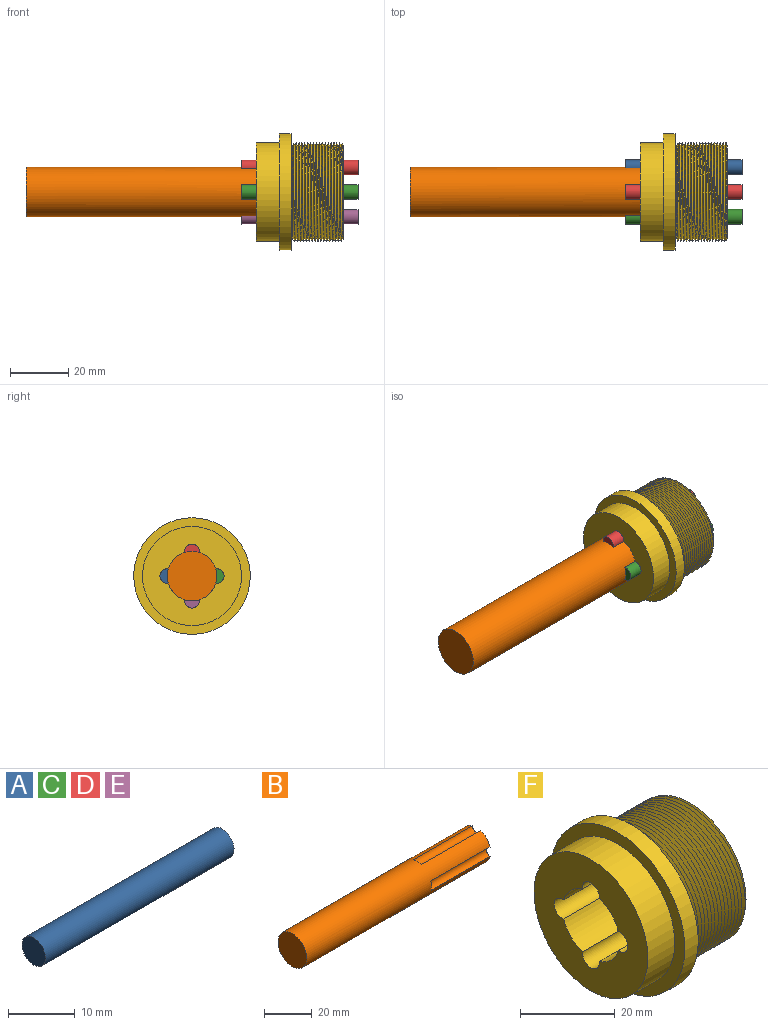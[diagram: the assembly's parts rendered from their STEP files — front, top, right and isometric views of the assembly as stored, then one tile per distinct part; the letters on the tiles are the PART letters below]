
ASSEMBLY  parts=6 mates=1
PART A: 3 faces, bbox 40x5x5 mm
  f0: cylinder r=2.5mm len=40mm, axis (-1,0,0), area 628.3mm2, adj f1,f2
  f1: plane 5x5mm, normal (1,0,0), area 19.6mm2, adj f0
  f2: plane 5x5mm, normal (-1,0,0), area 19.6mm2, adj f0
PART B: 11 faces, bbox 109x17x17 mm
  f0: plane 16.26x16.26mm, normal (1,0,0), area 190.2mm2, adj f1,f3,f5,f7,f9
  f1: cylinder r=8.5mm len=109mm, axis (-1,0,0), area 5118.8mm2, adj f0,f2,f3,f4,f5,f6,f7,f8
  f2: plane 17x17mm, normal (-1,0,0), area 227mm2, adj f1
  f3: cylinder r=2.5mm len=35mm, axis (1,0,0), area 249.1mm2, adj f0,f1,f4
  f4: plane 4.95x2.5mm, normal (1,0,0), area 9.2mm2, adj f1,f3
  f5: cylinder r=2.5mm len=35mm, axis (1,0,0), area 249.1mm2, adj f0,f1,f6
  f6: plane 4.95x2.5mm, normal (1,0,0), area 9.2mm2, adj f1,f5
  f7: cylinder r=2.5mm len=35mm, axis (1,0,0), area 249.1mm2, adj f0,f1,f8
  f8: plane 4.95x2.5mm, normal (1,0,0), area 9.2mm2, adj f1,f7
  f9: cylinder r=2.5mm len=35mm, axis (1,0,0), area 249.1mm2, adj f0,f1,f10
  f10: plane 4.95x2.5mm, normal (1,0,0), area 9.2mm2, adj f1,f9
PART C: same geometry as A
PART D: same geometry as A
PART E: same geometry as A
PART F: 19 faces, bbox 30.7x40x40 mm
  f0: plane 32x32mm, normal (1,0,0), area 535.5mm2, adj f3,f4,f5,f11,f12,f13,f14,f15
  f1: bspline ~39.26x34mm, area 1956.4mm2, adj f2,f16,f17
  f2: bspline ~39.26x34mm, area 1970.7mm2, adj f1,f16,f17
  f3: cylinder r=8.5mm len=30mm, axis (-1,0,0), area 250mm2, adj f0,f10,f12,f15
  f4: cylinder r=8.5mm len=30mm, axis (-1,0,0), area 250mm2, adj f0,f10,f14,f15
  f5: cylinder r=8.5mm len=30mm, axis (-1,0,0), area 250mm2, adj f0,f10,f13,f14
  f6: plane 40x40mm, normal (1,0,0), area 348.7mm2, adj f7,f18
  f7: cylinder r=20mm len=40mm, axis (-1,0,0), area 502.7mm2, adj f6,f8
  f8: plane 40x40mm, normal (-1,0,0), area 348.7mm2, adj f7,f9
  f9: cylinder r=17mm len=34mm, axis (-1,0,0), area 854.5mm2, adj f8,f10
  f10: plane 34x34mm, normal (-1,0,0), area 639.2mm2, adj f3,f4,f5,f9,f11,f12,f13,f14
  f11: cylinder r=8.5mm len=30mm, axis (-1,0,0), area 250mm2, adj f0,f10,f12,f13
  f12: cylinder r=2.5mm len=30mm, axis (1,0,0), area 257.8mm2, adj f0,f3,f10,f11
  f13: cylinder r=2.5mm len=30mm, axis (1,0,0), area 257.8mm2, adj f0,f5,f10,f11
  f14: cylinder r=2.5mm len=30mm, axis (1,0,0), area 257.8mm2, adj f0,f4,f5,f10
  f15: cylinder r=2.5mm len=30mm, axis (1,0,0), area 257.8mm2, adj f0,f3,f4,f10
  f16: cone r=17mm half-angle=63.4deg, axis (-1,0,0), area 57.4mm2, adj f0,f1,f2
  f17: cone r=17mm half-angle=63.4deg, axis (1,0,0), area 57.4mm2, adj f1,f2,f18
  f18: cone r=16mm half-angle=63.4deg, axis (-1,0,0), area 115.9mm2, adj f6,f17
PLACE A rot(axis=(-1,0,0),90deg) t=(-35,1.03,-21.46)mm
PLACE B at identity fixed
PLACE C rot(axis=(1,0,0),90deg) t=(-35,-1.03,21.46)mm
PLACE D t=(-35,21.46,1.03)mm
PLACE E rot(axis=(-1,0,0),180deg) t=(-35,-21.46,-1.03)mm
PLACE F at identity
MATE fastened D.f0 <-> B.f9  axis (-1,0,0) through (34,0,8.5)mm
